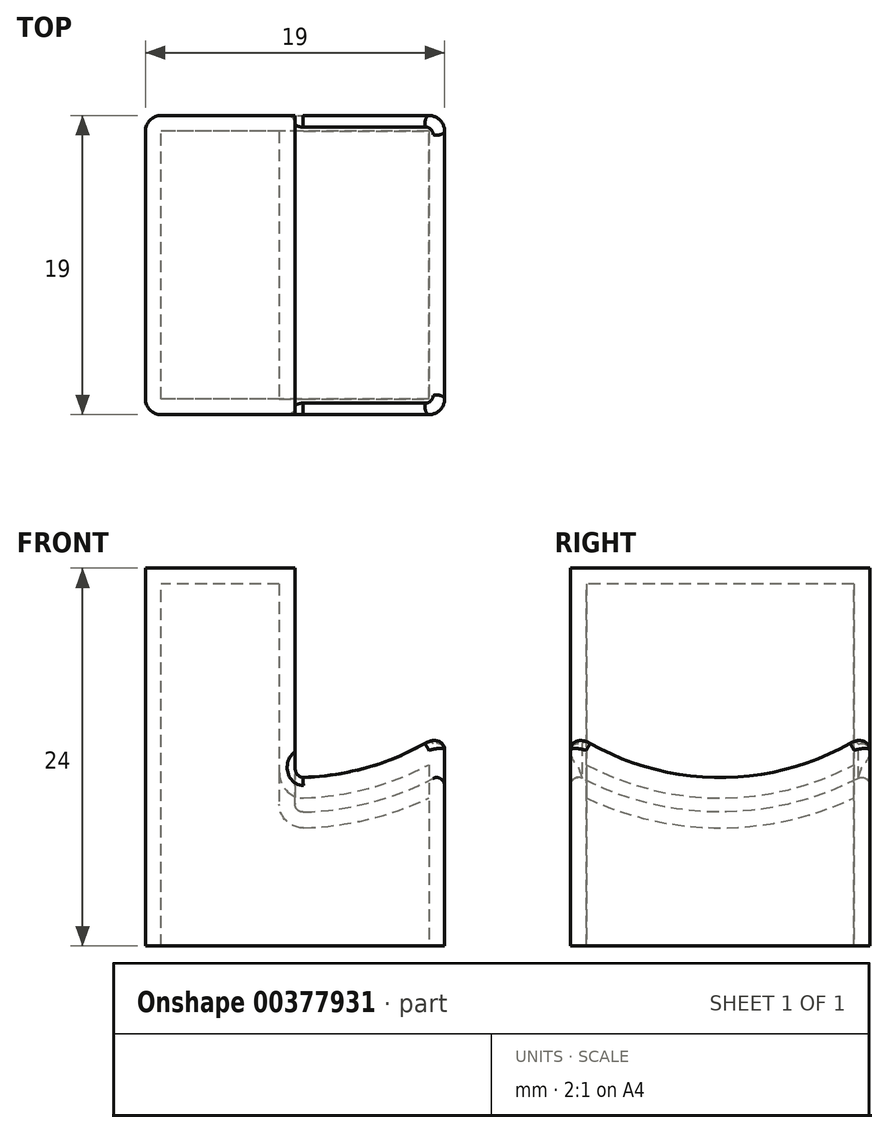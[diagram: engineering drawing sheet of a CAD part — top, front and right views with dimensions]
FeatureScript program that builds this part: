
annotation { "Feature Type Name" : "Feature", "Feature Type Description" : "" }
export const myFeature = defineFeature(function(context is Context, id is Id, definition is map)
    precondition{}
    {
        {
            var Q0;
            Q0=qCreatedBy(makeId("Top.planeOp"),FACE);
            var sketch = newSketch(context, id + "F0", { "sketchPlane" : qUnion([Q0])});
            skLineSegment(sketch, "E0.bottom", {"start": v(9.5, -9.5) * mm, "end": v(-9.5, -9.5) * mm});
            skLineSegment(sketch, "E0.top", {"start": v(9.5, 9.5) * mm, "end": v(-9.5, 9.5) * mm});
            skLineSegment(sketch, "E0.left", {"start": v(9.5, -9.5) * mm, "end": v(9.5, 9.5) * mm});
            skLineSegment(sketch, "E0.right", {"start": v(-9.5, -9.5) * mm, "end": v(-9.5, 9.5) * mm});
            skPoint(sketch, "E0.middle", {"position": v(0, 0) * mm});
            skSolve(sketch);
        }
        {
            var Q0;
            Q0=makeQuery(id+"F0.imprint","IMPRINT",FACE,{"disambiguationData":[TD([[makeQuery(id+"F0.imprint","IMPRINT",EDGE,{"derivedFrom":sQuery(id+"F0.wireOp",EDGE,"E0.bottom")}),-1.0]])]});
            extrude(context, id + "F1", {"entities" : qUnion([Q0]), "depth" : 25 * mm});
        }
        {
            var Q0;
            Q0=qCreatedBy(makeId("Front.planeOp"),FACE);
            var sketch = newSketch(context, id + "F2", { "sketchPlane" : qUnion([Q0])});
            skCircle(sketch, "E1", {"center": v(0, 28.5) * mm, "radius": 28.5 * mm, "construction": true});
            skCircle(sketch, "E2", {"center": v(0, 28.5) * mm, "radius": 19 * mm});
            skLineSegment(sketch, "E3", {"start": v(0, 0) * mm, "end": v(0, 28.5) * mm});
            skLineSegment(sketch, "E4", {"start": v(0, 28.5) * mm, "end": v(28.5, 28.5) * mm});
            skArc(sketch, "E5", {"start": v(0, 0) * mm, "mid": v(20.15, 8.35) * mm, "end": v(28.5, 28.5) * mm});
            skSolve(sketch);
        }
        {
            var Q0;
            {var subQ0=sQuery(id+"F2.wireOp",EDGE,"E3");var subQ1=sQuery(id+"F2.wireOp",EDGE,"E2");var subQ2=makeQuery(id+"F2.imprint","INTERSECT",VERTEX,{"derivedFrom":[subQ1,subQ0]});Q0=makeQuery(id+"F2.imprint","IMPRINT",FACE,{"disambiguationData":[TD([[makeQuery(id+"F2.imprint","IMPRINT",EDGE,{"disambiguationData":[TD([[subQ2,-1.0]])],"derivedFrom":subQ1}),1.0]])]});}
            var Q1;
            Q1=sQuery(id+"F2.wireOp",EDGE,"E4");
            revolve(context, id + "F3", {"operationType" : NewBodyOperationType.REMOVE, "entities" : qUnion([Q0]), "axis" : qUnion([Q1]), "revolveType" : RevolveType.FULL, "oppositeDirection" : true});
        }
        {
            var Q0;
            {var subQ0=sQuery(id+"F2.wireOp",EDGE,"E2");Q0=makeQuery(id+"FvMKDtnhoSPQzT9_1.2.F3.boolean.opBoolean","MERGE",FACE,{"derivedFrom":[makeQuery(id+"FvMKDtnhoSPQzT9_1.1.F3.boolean.opBoolean","MERGE",FACE,{"derivedFrom":[makeQuery(id+"F3.boolean.opBoolean","COPY",FACE,{"derivedFrom":makeQuery(id+"F3.opRevolve","SWEPT_FACE",FACE,{"disambiguationData":[OSD([subQ0])]})}),makeQuery(id+"FvMKDtnhoSPQzT9_1.1.F3.opRevolve","SWEPT_FACE",FACE,{"disambiguationData":[OSD([subQ0])]})]}),makeQuery(id+"FvMKDtnhoSPQzT9_1.2.F3.opRevolve","SWEPT_FACE",FACE,{"disambiguationData":[OSD([subQ0])]})]});}
            fillet(context, id + "F4", {"entities" : qUnion([Q0]), "radius" : 0.5 * mm, "tangentPropagation" : true, "allowEdgeOverflow" : false});
        }
        {
            var Q0;
            {var subQ0=sQuery(id+"F0.wireOp",EDGE,"E0.right");var subQ1=sQuery(id+"F0.wireOp",EDGE,"E0.top");Q0=makeQuery(id+"FsoDeZm5gfktgPt_1.3.FGidEBCg5Sp9znJ_1.boolean.opBoolean","SPLIT",EDGE,{"disambiguationData":[TD([makeQuery(id+"FsoDeZm5gfktgPt_1.3.FGidEBCg5Sp9znJ_1.opExtrude","SWEPT_FACE",FACE,{"disambiguationData":[OSD([sQuery(id+"FT4VpGubxb6nqfD_1.wireOp",EDGE,"53fbf8ce-7ae5-4f00-982d-1a8ac5a0b445")])]})])],"derivedFrom":makeQuery(id+"F1.opExtrude","SWEPT_EDGE",EDGE,{"disambiguationData":[OSD([subQ1,subQ0])]})});}
            var Q1;
            {var subQ1=sQuery(id+"F0.wireOp",EDGE,"E0.right");var subQ2=sQuery(id+"F0.wireOp",EDGE,"E0.top");Q1=makeQuery(id+"FsoDeZm5gfktgPt_1.3.FGidEBCg5Sp9znJ_1.boolean.opBoolean","SPLIT",EDGE,{"disambiguationData":[TD([makeQuery(id+"FsoDeZm5gfktgPt_1.3.FGidEBCg5Sp9znJ_1.opExtrude","SWEPT_FACE",FACE,{"disambiguationData":[OSD([sQuery(id+"FT4VpGubxb6nqfD_1.wireOp",EDGE,"2d1992d1-bf1c-4a19-a0c3-8986f30de3fd")])]})])],"derivedFrom":makeQuery(id+"F1.opExtrude","SWEPT_EDGE",EDGE,{"disambiguationData":[OSD([subQ2,subQ1])]})});}
            var Q2;
            {var subQ0=sQuery(id+"F0.wireOp",EDGE,"E0.left");var subQ1=sQuery(id+"F0.wireOp",EDGE,"E0.top");Q2=makeQuery(id+"FsoDeZm5gfktgPt_1.2.FGidEBCg5Sp9znJ_1.boolean.opBoolean","SPLIT",EDGE,{"disambiguationData":[TD([makeQuery(id+"FsoDeZm5gfktgPt_1.2.FGidEBCg5Sp9znJ_1.opExtrude","SWEPT_FACE",FACE,{"disambiguationData":[OSD([sQuery(id+"FT4VpGubxb6nqfD_1.wireOp",EDGE,"53fbf8ce-7ae5-4f00-982d-1a8ac5a0b445")])]})])],"derivedFrom":makeQuery(id+"F1.opExtrude","SWEPT_EDGE",EDGE,{"disambiguationData":[OSD([subQ1,subQ0])]})});}
            var Q3;
            {var subQ1=sQuery(id+"F0.wireOp",EDGE,"E0.left");var subQ2=sQuery(id+"F0.wireOp",EDGE,"E0.top");Q3=makeQuery(id+"FsoDeZm5gfktgPt_1.2.FGidEBCg5Sp9znJ_1.boolean.opBoolean","SPLIT",EDGE,{"disambiguationData":[TD([makeQuery(id+"FsoDeZm5gfktgPt_1.2.FGidEBCg5Sp9znJ_1.opExtrude","SWEPT_FACE",FACE,{"disambiguationData":[OSD([sQuery(id+"FT4VpGubxb6nqfD_1.wireOp",EDGE,"2d1992d1-bf1c-4a19-a0c3-8986f30de3fd")])]})])],"derivedFrom":makeQuery(id+"F1.opExtrude","SWEPT_EDGE",EDGE,{"disambiguationData":[OSD([subQ2,subQ1])]})});}
            var Q4;
            {var subQ0=sQuery(id+"F0.wireOp",EDGE,"E0.bottom");var subQ1=sQuery(id+"F0.wireOp",EDGE,"E0.left");Q4=makeQuery(id+"FsoDeZm5gfktgPt_1.1.FGidEBCg5Sp9znJ_1.boolean.opBoolean","SPLIT",EDGE,{"disambiguationData":[TD([makeQuery(id+"FsoDeZm5gfktgPt_1.1.FGidEBCg5Sp9znJ_1.opExtrude","SWEPT_FACE",FACE,{"disambiguationData":[OSD([sQuery(id+"FT4VpGubxb6nqfD_1.wireOp",EDGE,"53fbf8ce-7ae5-4f00-982d-1a8ac5a0b445")])]})])],"derivedFrom":makeQuery(id+"F1.opExtrude","SWEPT_EDGE",EDGE,{"disambiguationData":[OSD([subQ0,subQ1])]})});}
            var Q5;
            {var subQ1=sQuery(id+"F0.wireOp",EDGE,"E0.bottom");var subQ2=sQuery(id+"F0.wireOp",EDGE,"E0.left");Q5=makeQuery(id+"FsoDeZm5gfktgPt_1.1.FGidEBCg5Sp9znJ_1.boolean.opBoolean","SPLIT",EDGE,{"disambiguationData":[TD([makeQuery(id+"FsoDeZm5gfktgPt_1.1.FGidEBCg5Sp9znJ_1.opExtrude","SWEPT_FACE",FACE,{"disambiguationData":[OSD([sQuery(id+"FT4VpGubxb6nqfD_1.wireOp",EDGE,"2d1992d1-bf1c-4a19-a0c3-8986f30de3fd")])]})])],"derivedFrom":makeQuery(id+"F1.opExtrude","SWEPT_EDGE",EDGE,{"disambiguationData":[OSD([subQ1,subQ2])]})});}
            var Q6;
            {var subQ0=sQuery(id+"F0.wireOp",EDGE,"E0.bottom");var subQ1=sQuery(id+"F0.wireOp",EDGE,"E0.right");Q6=makeQuery(id+"FGidEBCg5Sp9znJ_1.boolean.opBoolean","SPLIT",EDGE,{"disambiguationData":[TD([makeQuery(id+"FGidEBCg5Sp9znJ_1.opExtrude","SWEPT_FACE",FACE,{"disambiguationData":[OSD([sQuery(id+"FT4VpGubxb6nqfD_1.wireOp",EDGE,"53fbf8ce-7ae5-4f00-982d-1a8ac5a0b445")])]})])],"derivedFrom":makeQuery(id+"F1.opExtrude","SWEPT_EDGE",EDGE,{"disambiguationData":[OSD([subQ0,subQ1])]})});}
            var Q7;
            {var subQ1=sQuery(id+"F0.wireOp",EDGE,"E0.bottom");var subQ2=sQuery(id+"F0.wireOp",EDGE,"E0.right");Q7=makeQuery(id+"FGidEBCg5Sp9znJ_1.boolean.opBoolean","SPLIT",EDGE,{"disambiguationData":[TD([makeQuery(id+"FGidEBCg5Sp9znJ_1.opExtrude","SWEPT_FACE",FACE,{"disambiguationData":[OSD([sQuery(id+"FT4VpGubxb6nqfD_1.wireOp",EDGE,"2d1992d1-bf1c-4a19-a0c3-8986f30de3fd")])]})])],"derivedFrom":makeQuery(id+"F1.opExtrude","SWEPT_EDGE",EDGE,{"disambiguationData":[OSD([subQ1,subQ2])]})});}
            fillet(context, id + "F5", {"entities" : qUnion([Q0, Q1, Q2, Q3, Q4, Q5, Q6, Q7]), "radius" : 1 * mm, "tangentPropagation" : true, "allowEdgeOverflow" : false});
        }
        {
            var Q0;
            Q0=makeQuery(id+"F1.opExtrude","CAP_FACE",FACE,{"disambiguationData":[OSD([sQuery(id+"F0.wireOp",EDGE,"E0.bottom"),sQuery(id+"F0.wireOp",EDGE,"E0.top"),sQuery(id+"F0.wireOp",EDGE,"E0.left"),sQuery(id+"F0.wireOp",EDGE,"E0.right")])],"isStart":true});
            shell(context, id + "F6", {"entities" : qUnion([Q0]), "thickness" : 1 * mm});
        }
        {
            var Q0;
            Q0=makeQuery(id+"F0.imprint","IMPRINT",FACE,{"disambiguationData":[TD([[makeQuery(id+"F0.imprint","IMPRINT",EDGE,{"derivedFrom":sQuery(id+"F0.wireOp",EDGE,"E0.bottom")}),-1.0]])]});
            extrude(context, id + "F7", {"entities" : qUnion([Q0]), "operationType" : NewBodyOperationType.REMOVE, "depth" : 1 * mm});
        }
    });
